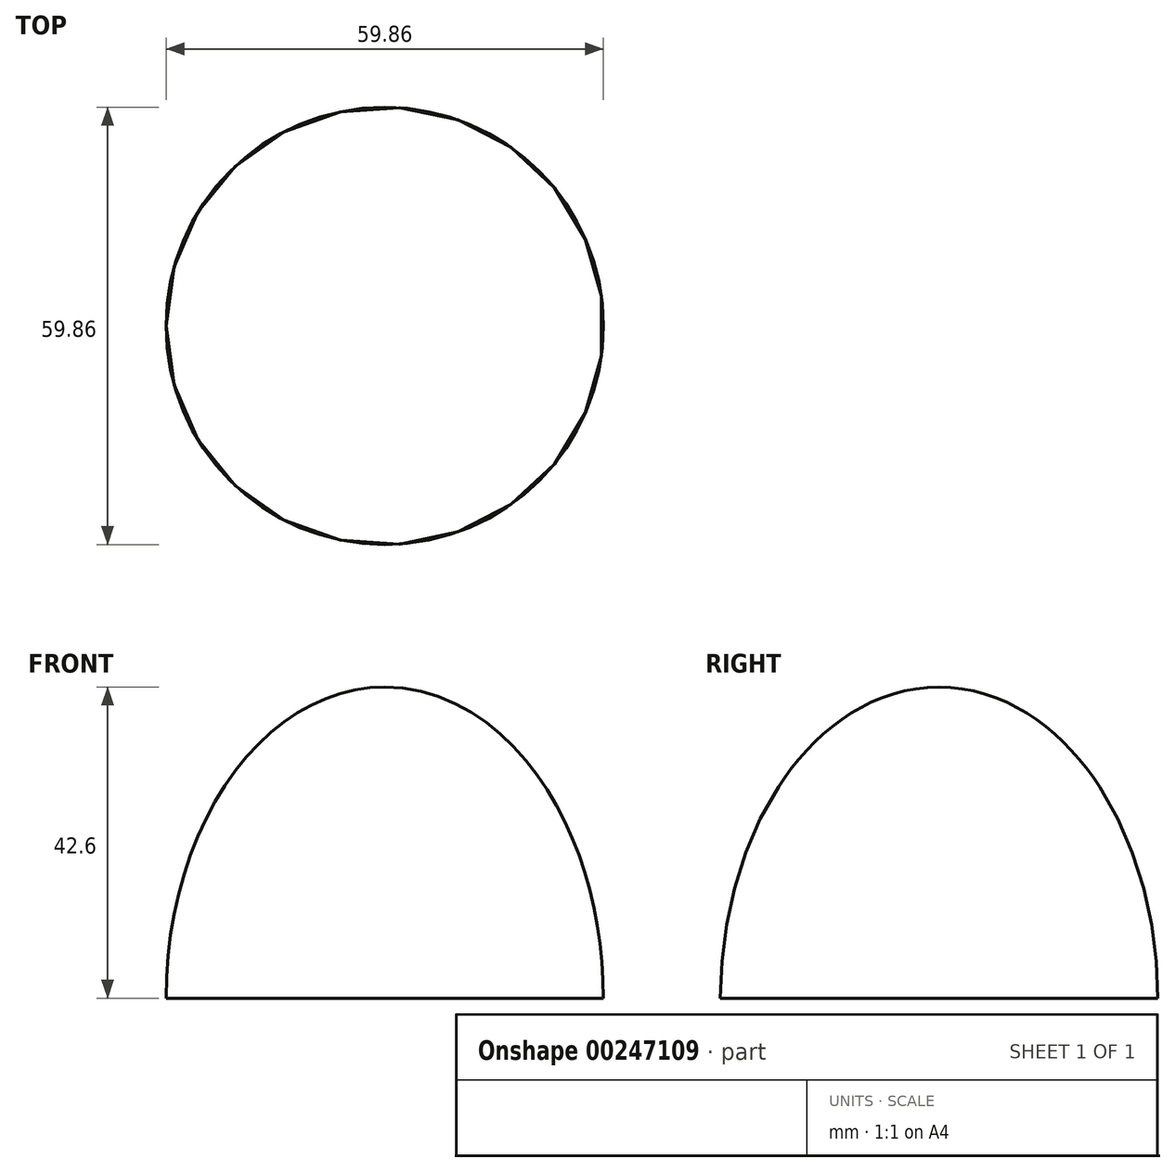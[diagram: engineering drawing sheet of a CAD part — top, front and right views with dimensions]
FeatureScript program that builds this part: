
annotation { "Feature Type Name" : "Feature", "Feature Type Description" : "" }
export const myFeature = defineFeature(function(context is Context, id is Id, definition is map)
    precondition{}
    {
        {
            var Q0;
            Q0=qCreatedBy(makeId("Front.planeOp"),FACE);
            var sketch = newSketch(context, id + "F0", { "sketchPlane" : qUnion([Q0])});
            skEllipticalArc(sketch, "E0", {});
            skLineSegment(sketch, "E1", {"start": v(-29.93, 0) * mm, "end": v(0, 0) * mm});
            skLineSegment(sketch, "E2", {"start": v(0, 42.6) * mm, "end": v(0, 0) * mm});
            skPoint(sketch, "E3.orphan", {"position": v(29.93, 0) * mm});
            const initialGuessF0  = {"E0": [0, 0, 0, 1, 0.04259525239467621, 0.029931798577308655, 0, 1.5707963267948966]};
            skSetInitialGuess(sketch, initialGuessF0);
            skSolve(sketch);
        }
        {
            var Q0;
            Q0=makeQuery(id+"F0.imprint","IMPRINT",FACE,{"disambiguationData":[TD([[makeQuery(id+"F0.imprint","IMPRINT",EDGE,{"derivedFrom":sQuery(id+"F0.wireOp",EDGE,"E0")}),1.0]])]});
            var Q1;
            Q1=sQuery(id+"F0.wireOp",EDGE,"E2");
            revolve(context, id + "F1", {"entities" : qUnion([Q0]), "axis" : qUnion([Q1]), "revolveType" : RevolveType.FULL});
        }
    });
